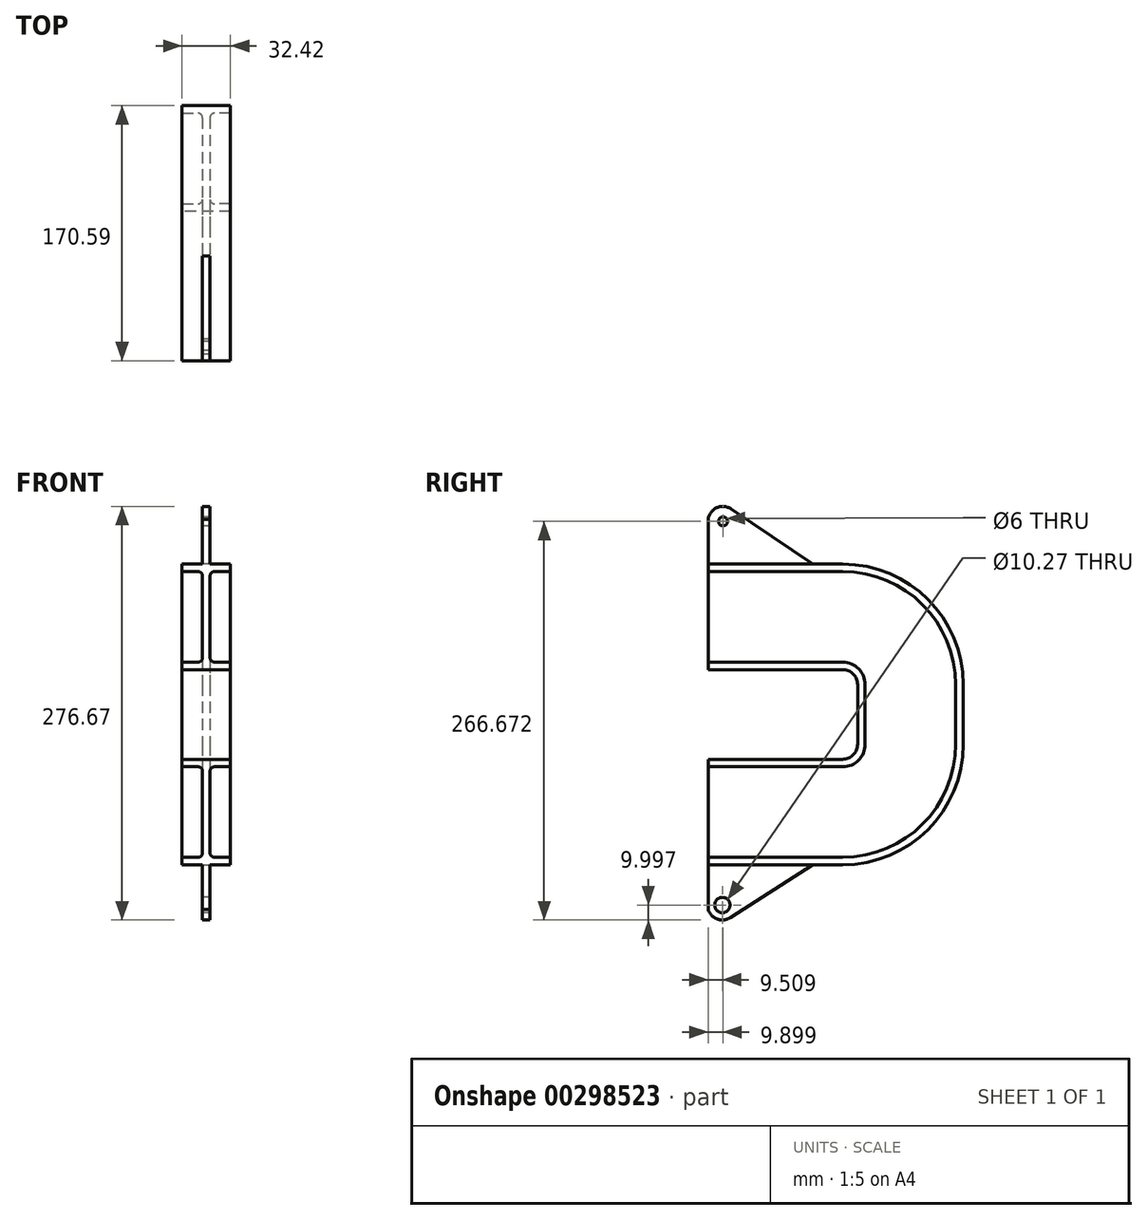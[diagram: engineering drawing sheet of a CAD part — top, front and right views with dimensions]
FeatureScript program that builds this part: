
annotation { "Feature Type Name" : "Feature", "Feature Type Description" : "" }
export const myFeature = defineFeature(function(context is Context, id is Id, definition is map)
    precondition{}
    {
        {
            var Q0;
            Q0=qCreatedBy(makeId("Front.planeOp"),FACE);
            var sketch = newSketch(context, id + "F0", { "sketchPlane" : qUnion([Q0])});
            skLineSegment(sketch, "E0", {"start": v(0, 35.3) * mm, "end": v(16.21, 35.3) * mm});
            skLineSegment(sketch, "E1", {"start": v(16.21, 35.3) * mm, "end": v(16.21, 30.3) * mm});
            skLineSegment(sketch, "E2", {"start": v(16.21, 30.3) * mm, "end": v(5.5, 30.3) * mm});
            skLineSegment(sketch, "E3", {"start": v(2.5, 27.3) * mm, "end": v(2.5, 0) * mm});
            skPoint(sketch, "E4.visualSharp", {"position": v(2.5, 30.3) * mm});
            skArc(sketch, "E4.filletArc", {"start": v(5.5, 30.3) * mm, "mid": v(3.38, 29.42) * mm, "end": v(2.5, 27.3) * mm});
            skLineSegment(sketch, "E5.MirrorCS", {"start": v(-16.21, 30.3) * mm, "end": v(-5.5, 30.3) * mm});
            skArc(sketch, "E6.MirrorCS", {"start": v(-5.5, 30.3) * mm, "mid": v(-3.38, 29.42) * mm, "end": v(-2.5, 27.3) * mm});
            skLineSegment(sketch, "E7.MirrorCS", {"start": v(0, 35.3) * mm, "end": v(-16.21, 35.3) * mm});
            skLineSegment(sketch, "E8.MirrorCS", {"start": v(-16.21, 35.3) * mm, "end": v(-16.21, 30.3) * mm});
            skPoint(sketch, "E9.MirrorP", {"position": v(-2.5, 30.3) * mm});
            skLineSegment(sketch, "E10.MirrorCS", {"start": v(-2.5, 27.3) * mm, "end": v(-2.5, 0) * mm});
            skLineSegment(sketch, "E11.MirrorCS", {"start": v(-16.21, -30.3) * mm, "end": v(-5.5, -30.3) * mm});
            skLineSegment(sketch, "E12.MirrorCS", {"start": v(16.21, -30.3) * mm, "end": v(5.5, -30.3) * mm});
            skArc(sketch, "E13.MirrorCS", {"start": v(-5.5, -30.3) * mm, "mid": v(-3.38, -29.42) * mm, "end": v(-2.5, -27.3) * mm});
            skArc(sketch, "E14.MirrorCS", {"start": v(5.5, -30.3) * mm, "mid": v(3.38, -29.42) * mm, "end": v(2.5, -27.3) * mm});
            skPoint(sketch, "E15.MirrorP", {"position": v(-2.5, -30.3) * mm});
            skLineSegment(sketch, "E16.MirrorCS", {"start": v(-2.5, -27.3) * mm, "end": v(-2.5, 0) * mm});
            skLineSegment(sketch, "E17.MirrorCS", {"start": v(-16.21, -35.3) * mm, "end": v(-16.21, -30.3) * mm});
            skLineSegment(sketch, "E18.MirrorCS", {"start": v(0, -35.3) * mm, "end": v(-16.21, -35.3) * mm});
            skLineSegment(sketch, "E19.MirrorCS", {"start": v(16.21, -35.3) * mm, "end": v(16.21, -30.3) * mm});
            skPoint(sketch, "E20.MirrorP", {"position": v(2.5, -30.3) * mm});
            skLineSegment(sketch, "E21.MirrorCS", {"start": v(2.5, -27.3) * mm, "end": v(2.5, 0) * mm});
            skLineSegment(sketch, "E22.MirrorCS", {"start": v(0, -35.3) * mm, "end": v(16.21, -35.3) * mm});
            skSolve(sketch);
        }
        {
            var Q0;
            Q0=qCreatedBy(makeId("Right.planeOp"),FACE);
            var sketch = newSketch(context, id + "F1", { "sketchPlane" : qUnion([Q0])});
            skLineSegment(sketch, "E23", {"start": v(0, -35.3) * mm, "end": v(90, -35.3) * mm});
            skLineSegment(sketch, "E24", {"start": v(100, -45.3) * mm, "end": v(100, -85.3) * mm});
            skLineSegment(sketch, "E25", {"start": v(90, -95.3) * mm, "end": v(0, -95.3) * mm});
            skPoint(sketch, "E26.visualSharp", {"position": v(100, -35.3) * mm});
            skArc(sketch, "E26.filletArc", {"start": v(100, -45.3) * mm, "mid": v(97.07, -38.23) * mm, "end": v(90, -35.3) * mm});
            skPoint(sketch, "E27.visualSharp", {"position": v(100, -95.3) * mm});
            skArc(sketch, "E27.filletArc", {"start": v(90, -95.3) * mm, "mid": v(97.07, -92.37) * mm, "end": v(100, -85.3) * mm});
            skSolve(sketch);
        }
        {
            var Q0;
            Q0=qSketchRegion(id+"F0",true);
            var Q1;
            Q1=qConstructionFilter(qBodyType(qCreatedBy(id+"F1",EDGE),BodyType.WIRE),ConstructionObject.NO);
            sweep(context, id + "F2", {"profiles" : qUnion([Q0]), "path" : qUnion([Q1])});
        }
        {
            var Q0;
            Q0=qCreatedBy(makeId("Right.planeOp"),FACE);
            var sketch = newSketch(context, id + "F3", { "sketchPlane" : qUnion([Q0])});
            skLineSegment(sketch, "E28", {"start": v(0, 35.3) * mm, "end": v(70, 35.3) * mm});
            skLineSegment(sketch, "E29", {"start": v(70, 35.3) * mm, "end": v(0, 35.3) * mm});
            skLineSegment(sketch, "E30", {"start": v(70, 35.3) * mm, "end": v(15.5, 72.16) * mm});
            skArc(sketch, "E31", {"start": v(15.5, 72.16) * mm, "mid": v(5.85, 73.02) * mm, "end": v(0, 65.3) * mm});
            skLineSegment(sketch, "E32", {"start": v(0, 65.3) * mm, "end": v(0, 35.3) * mm});
            skCircle(sketch, "E33", {"center": v(9.9, 63.88) * mm, "radius": 3 * mm});
            skSolve(sketch);
        }
        {
            var Q0;
            Q0=qSketchRegion(id+"F3",true);
            extrude(context, id + "F4", {"entities" : qUnion([Q0]), "operationType" : NewBodyOperationType.ADD, "endBound" : BoundingType.SYMMETRIC, "depth" : 5 * mm});
        }
        {
            var Q0;
            Q0=qCreatedBy(makeId("Right.planeOp"),FACE);
            var sketch = newSketch(context, id + "F5", { "sketchPlane" : qUnion([Q0])});
            skLineSegment(sketch, "E34", {"start": v(0, -165.89) * mm, "end": v(70, -165.89) * mm});
            skLineSegment(sketch, "E35", {"start": v(70, -165.89) * mm, "end": v(14.9, -201.21) * mm});
            skArc(sketch, "E36", {"start": v(14.9, -201.21) * mm, "mid": v(6.15, -202.21) * mm, "end": v(0, -195.89) * mm});
            skLineSegment(sketch, "E37", {"start": v(0, -165.89) * mm, "end": v(0, -195.89) * mm});
            skCircle(sketch, "E38", {"center": v(9.5, -192.8) * mm, "radius": 5.13 * mm});
            skSolve(sketch);
        }
        {
            var Q0;
            Q0=qSketchRegion(id+"F5",true);
            extrude(context, id + "F6", {"entities" : qUnion([Q0]), "operationType" : NewBodyOperationType.ADD, "endBound" : BoundingType.SYMMETRIC, "depth" : 5 * mm});
        }
    });
